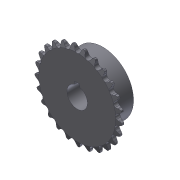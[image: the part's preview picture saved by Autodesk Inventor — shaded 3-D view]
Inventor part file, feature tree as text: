
AUTODESK INVENTOR PART (.ipt)
format: ipt  version: 2012 (Build 160160000, 160)  size: 668,672 bytes
history: native  units: in
note: dims shown in document units (in); Inventor stores cm internally (conversion verified against a paired STEP export)
features: other x2, extrude x2, sketch x2, imported_body x1
ambient origin geometry x8: Origin, YZ Plane, XZ Plane, XY Plane, X Axis, Y Axis, Z Axis, Center Point
feature tree (7):
  parser-record x1  (decoder bookkeeping rows leaked as tree rows — omitted from the tree; the rows remain in map.json)
  other  "6793K1801"
  extrude  "Extrusion1"  Depth=1.0in TaperAngle=0.0deg
  extrude  "Extrusion2"  Depth=0.125in
  imported_body  "Base1"
  sketch  "Sketch1"  dims[d0=0.5in d1=1.0in d2=0.0in]
  sketch  "Sketch2"  dims[d3=0.0625in d4=0.125in d5=1.0in d6=0.0in]
